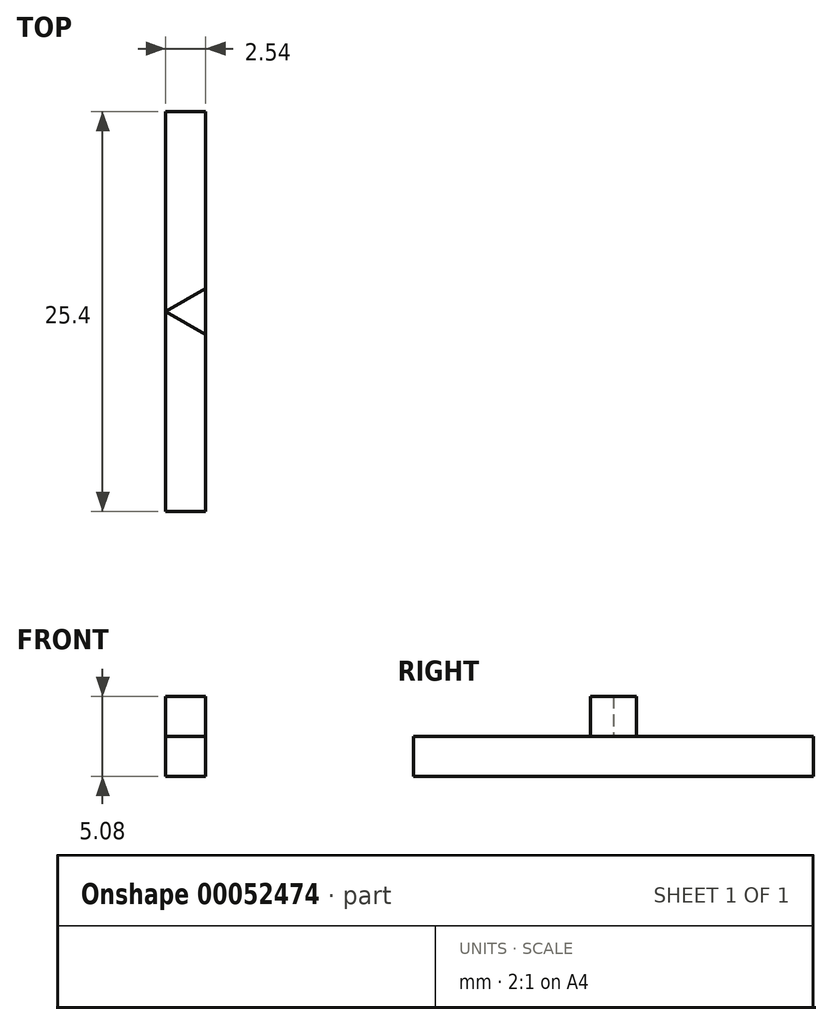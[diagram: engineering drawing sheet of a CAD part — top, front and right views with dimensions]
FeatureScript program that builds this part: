
annotation { "Feature Type Name" : "Feature", "Feature Type Description" : "" }
export const myFeature = defineFeature(function(context is Context, id is Id, definition is map)
    precondition{}
    {
        {
            var Q0;
            Q0=qCreatedBy(makeId("Top.planeOp"),FACE);
            var sketch = newSketch(context, id + "F0", { "sketchPlane" : qUnion([Q0])});
            skLineSegment(sketch, "E0.bottom", {"start": v(0, 25.4) * mm, "end": v(2.54, 25.4) * mm});
            skLineSegment(sketch, "E0.top", {"start": v(0, 0) * mm, "end": v(2.54, 0) * mm});
            skLineSegment(sketch, "E0.left", {"start": v(0, 25.4) * mm, "end": v(0, 0) * mm});
            skLineSegment(sketch, "E0.right", {"start": v(2.54, 25.4) * mm, "end": v(2.54, 0) * mm});
            skSolve(sketch);
        }
        {
            var Q0;
            Q0=makeQuery(id+"F0.imprint","IMPRINT",FACE,{"disambiguationData":[TD([[makeQuery(id+"F0.imprint","IMPRINT",EDGE,{"derivedFrom":sQuery(id+"F0.wireOp",EDGE,"E0.bottom")}),-1.0]])]});
            extrude(context, id + "F1", {"entities" : qUnion([Q0]), "oppositeDirection" : true, "depth" : 2.54 * mm});
        }
        {
            var Q0;
            Q0=qCreatedBy(makeId("Top.planeOp"),FACE);
            var sketch = newSketch(context, id + "F2", { "sketchPlane" : qUnion([Q0])});
            skLineSegment(sketch, "E1", {"start": v(2.54, 14.17) * mm, "end": v(2.54, 11.23) * mm});
            skLineSegment(sketch, "E2", {"start": v(2.54, 11.23) * mm, "end": v(0, 12.7) * mm});
            skLineSegment(sketch, "E3", {"start": v(0, 12.7) * mm, "end": v(2.54, 14.17) * mm});
            skSolve(sketch);
        }
        {
            var Q0;
            Q0 = qSketchRegion(id + "F2", true);
            extrude(context, id + "F3", {"entities" : qUnion([Q0]), "depth" : 2.54 * mm});
        }
    });
